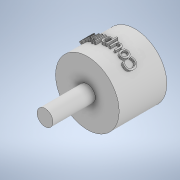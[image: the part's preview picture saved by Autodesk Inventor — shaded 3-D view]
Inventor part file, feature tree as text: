
AUTODESK INVENTOR PART (.ipt)
format: ipt  version: 2021 (Build 250183000, 183)  size: 428,544 bytes
history: native  units: mm
features: sketch x6, extrude x3, loft x1, plane x1, emboss x1
ambient origin geometry x8: Origin, YZ Plane, XZ Plane, XY Plane, X Axis, Y Axis, Z Axis, Center Point
bodies: Body1 (feature_tree)
feature tree (12):
  extrude  "Extrusion4"  Depth=7.0mm TaperAngle=0.0deg
  loft  "Loft3"
  extrude  "Extrusion5"  Depth=2.5mm
  extrude  "Extrusion6"  Depth=6.0mm
  plane  "Work Plane4"
  emboss  "Emboss1"
  sketch  "Sketch8"  dims[d35=12.0mm d36=7.0mm d37=0.0mm]
  sketch  "Sketch9"  dims[d38=5.0mm d39=5.0mm]
  sketch  "Sketch10"  dims[d40=2.5mm d41=2.5mm]
  sketch  "Sketch11"  dims[d42=6.0mm d43=6.0mm]
  sketch  "Sketch12"  dims[d44=3.0mm]
  sketch  "Sketch16"  dims[d45=3.0mm d46=0.0mm d47=90.0deg d48=0.0mm d49=90.0deg d50=2.0mm d51=0.0mm d52=3.0mm d53=8.0mm d54=0.0mm d63=7.0mm d64=0.5mm d65=0.0mm d22=0.5mm d23=0.872665mm d24=0.5mm d25=0.872665mm]
